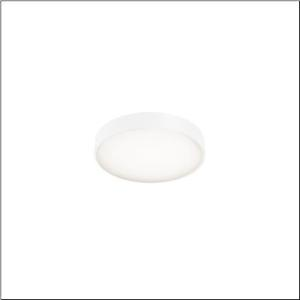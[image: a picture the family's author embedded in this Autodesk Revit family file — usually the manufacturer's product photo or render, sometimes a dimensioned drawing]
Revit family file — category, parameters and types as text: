
# Revit family: round_21_s_51mr34gd0421w
name_source: partatom
category: Lighting Fixtures
units: mm (PartAtom-declared; Revit-internal decimal feet)

## family parameters
Cut with Voids When Loaded = No
Host = Face
Light Source = No
Part Type = Normal
Room Calculation Point = No
Round Connector Dimension = Use Diameter
Shared = No

## types (1)
- Round 21 S (1 x LED, 3490 lm, 28 W, 4000K)
    Apparent Load = 28 VA
    CIE Flux Codes = 49 80 96 79 100
    Color Rendering = 80
    Color Temperature = 4000K
    Default Elevation = 1800 mm
    Description = Round 21 S, wall and ceiling luminaire, primary optical cover: cover, of PMMA, opal, light emission: direct/indirect distribution, primary light characteristic: symmetric, installation type: suspended mounting, surface-mounted, LED, rated luminous flux: 3.580lm, luminous efficacy: 118lm/W, light colour: 840, colour temperature: 4000K, with terminal, 5-pole, mains connection: 230V, AC, 50/60Hz, rated input power: 30W, housing, of aluminium, coated, white, diameter: 400mm, height: 62mm, protection rating (complete): IP40, insulation class (complete): insulation class I (protective earthing), certification: CE, impact resistance: IK04, permissible operating ambient temperature: -10..+35°C, packaging unit: 1 piece
    Height = 87 mm
    Lamp = 1 x LED
    Lamp Light Flux = 3490 lm
    Lamp Power = 28 W
    Lamp count = 1
    Length = 400 mm
    Luminous efficacy = 125 lm/W
    Manufacturer = Siteco
    ModVariant = No
    Model = 51MR34GD0421W
    Mounting Place = Ceiling
    Mounting Type = Surface mounted
    Number of Poles = 1
    OnlyDefault = Yes
    Power Factor = 1
    Product Name = Round 21 S
    Product group = wall and ceiling luminaire
    ProductGroupID = 301
    Protection Class = Protection class I
    Protection Degree = IP 40
    RLX_Detail_Level = 1
    RLX_Emergency_Light_Flux = 0 lm
    RLX_Emergency_Type = 0
    RLX_Emergency_Type_DB = No
    RlxData = <blob elided: 9905 chars, md5=fe98a569>
    Socket = socket
    Standby Power = 0 W
    System Light Flux = 3490 lm
    System Power = 28 W
    Type Comments = Product without accessories
    Type Image = l_1258307.jpg
    URL = http://relux.com
    VarID = ---
    Voltage = 0 V
    Weight = 0.00 kg
    Width = 0 mm  [stored 0 ft]

note: [stored X ft] marks values corroborated as IEEE doubles in the binary element streams (Revit-internal decimal feet)

## geometry (parser evidence)
native form markers: Sweep x12
no freeform markers — native parametric forms only
